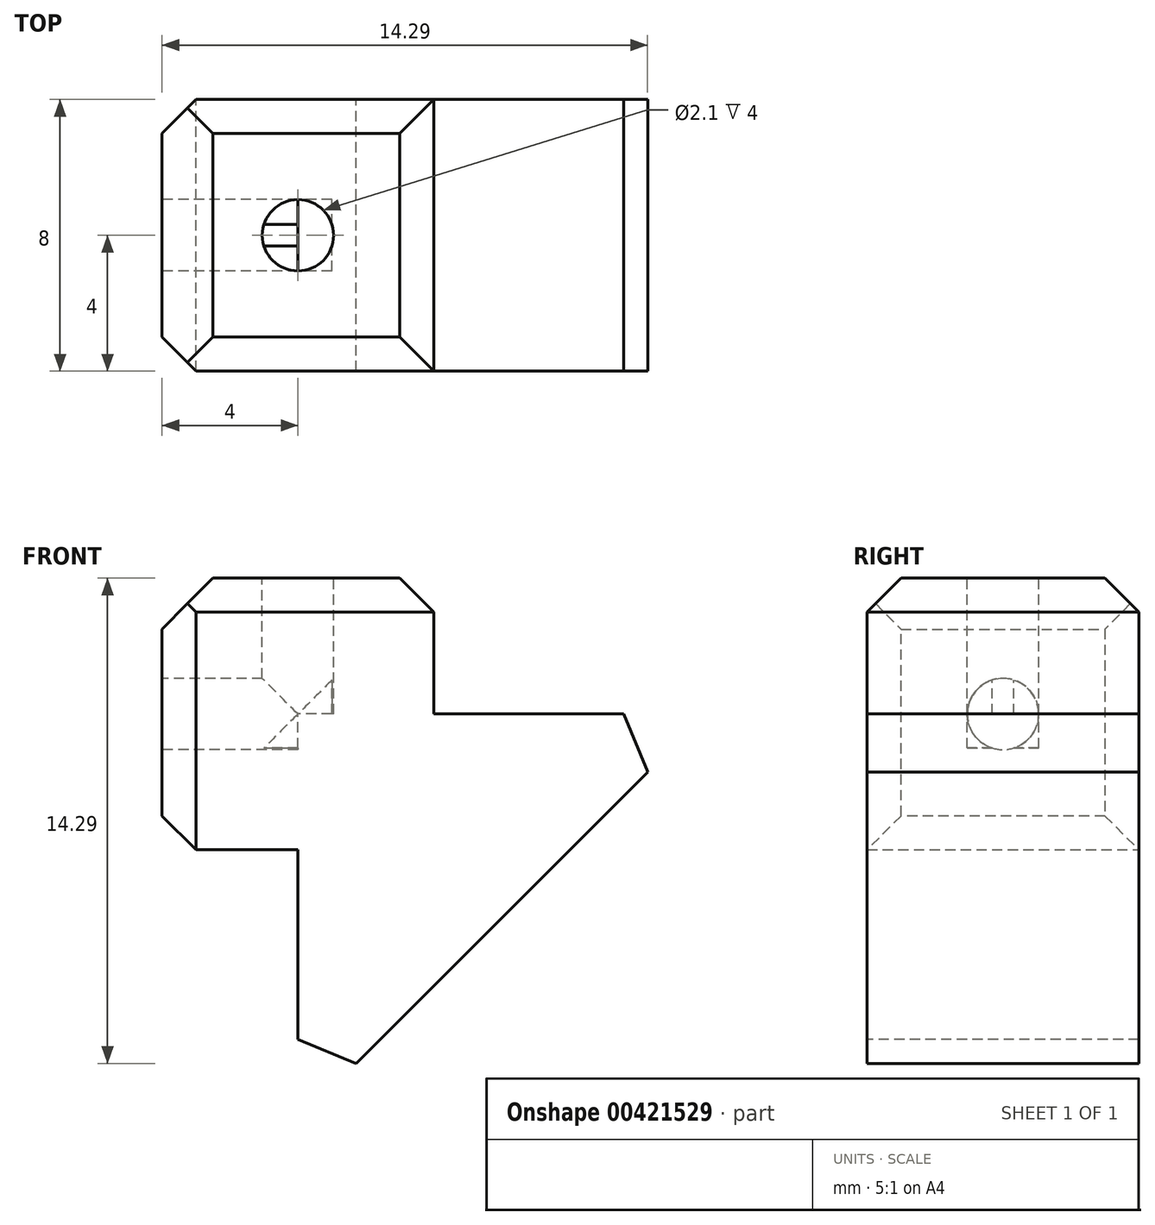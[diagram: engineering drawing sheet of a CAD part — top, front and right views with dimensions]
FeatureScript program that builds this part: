
annotation { "Feature Type Name" : "Feature", "Feature Type Description" : "" }
export const myFeature = defineFeature(function(context is Context, id is Id, definition is map)
    precondition{}
    {
        {
            var Q0;
            Q0=qCreatedBy(makeId("Front.planeOp"),FACE);
            var sketch = newSketch(context, id + "F0", { "sketchPlane" : qUnion([Q0])});
            skLineSegment(sketch, "E0.bottom", {"start": v(4, -4) * mm, "end": v(-4, -4) * mm});
            skLineSegment(sketch, "E0.top", {"start": v(4, 4) * mm, "end": v(-4, 4) * mm});
            skLineSegment(sketch, "E0.left", {"start": v(4, -4) * mm, "end": v(4, 4) * mm});
            skLineSegment(sketch, "E0.right", {"start": v(-4, -4) * mm, "end": v(-4, 4) * mm});
            skPoint(sketch, "E0.middle", {"position": v(0, 0) * mm});
            skSolve(sketch);
        }
        {
            var Q0;
            Q0=makeQuery(id+"F0.imprint","IMPRINT",FACE,{"disambiguationData":[TD([[makeQuery(id+"F0.imprint","IMPRINT",EDGE,{"derivedFrom":sQuery(id+"F0.wireOp",EDGE,"E0.bottom")}),-1.0]])]});
            extrude(context, id + "F1", {"entities" : qUnion([Q0]), "depth" : 8 * mm, "offsetDistance" : 25 * mm, "symmetric" : true});
        }
        {
            var Q0;
            Q0=makeQuery(id+"F1.opExtrude","SWEPT_FACE",FACE,{"disambiguationData":[OSD([sQuery(id+"F0.wireOp",EDGE,"E0.top")])]});
            var sketch = newSketch(context, id + "F2", { "sketchPlane" : qUnion([Q0])});
            skCircle(sketch, "E1", {"center": v(0, 0) * mm, "radius": 1.05 * mm});
            skSolve(sketch);
        }
        {
            var Q0;
            Q0=makeQuery(id+"F2.imprint","IMPRINT",FACE,{"disambiguationData":[TD([[makeQuery(id+"F2.imprint","IMPRINT",EDGE,{"derivedFrom":sQuery(id+"F2.wireOp",EDGE,"E1")}),1.0]])]});
            extrude(context, id + "F3", {"entities" : qUnion([Q0]), "operationType" : NewBodyOperationType.REMOVE, "oppositeDirection" : true, "depth" : 5 * mm, "offsetDistance" : 25 * mm});
        }
        {
            var Q0;
            Q0=makeQuery(id+"F1.opExtrude","SWEPT_FACE",FACE,{"disambiguationData":[OSD([sQuery(id+"F0.wireOp",EDGE,"E0.right")])]});
            var sketch = newSketch(context, id + "F4", { "sketchPlane" : qUnion([Q0])});
            skCircle(sketch, "E2", {"center": v(0, 0) * mm, "radius": 1.05 * mm});
            skSolve(sketch);
        }
        {
            var Q0;
            Q0=makeQuery(id+"F4.imprint","IMPRINT",FACE,{"disambiguationData":[TD([[makeQuery(id+"F4.imprint","IMPRINT",EDGE,{"derivedFrom":sQuery(id+"F4.wireOp",EDGE,"E2")}),1.0]])]});
            extrude(context, id + "F5", {"entities" : qUnion([Q0]), "operationType" : NewBodyOperationType.REMOVE, "oppositeDirection" : true, "depth" : 5 * mm, "offsetDistance" : 25 * mm});
        }
        {
            var Q0;
            Q0=makeQuery(id+"F1.opExtrude","SWEPT_EDGE",EDGE,{"disambiguationData":[OSD([sQuery(id+"F0.wireOp",EDGE,"E0.top"),sQuery(id+"F0.wireOp",EDGE,"E0.right")])]});
            chamfer(context, id + "F6", {"entities" : qUnion([Q0]), "width" : 1.5 * mm, "tangentPropagation" : true});
        }
        {
            var Q0;
            Q0=qCreatedBy(makeId("Front.planeOp"),FACE);
            var sketch = newSketch(context, id + "F7", { "sketchPlane" : qUnion([Q0])});
            skLineSegment(sketch, "E3.bottom", {"start": v(0, 0) * mm, "end": v(12, 0) * mm});
            skLineSegment(sketch, "E3.left", {"start": v(0, 0) * mm, "end": v(0, -12) * mm});
            skLineSegment(sketch, "E4", {"start": v(0, -12) * mm, "end": v(12, 0) * mm});
            skSolve(sketch);
        }
        {
            var Q0;
            Q0=makeQuery(id+"F7.imprint","IMPRINT",FACE,{"disambiguationData":[TD([[makeQuery(id+"F7.imprint","IMPRINT",EDGE,{"derivedFrom":sQuery(id+"F7.wireOp",EDGE,"E3.bottom")}),-1.0]])]});
            extrude(context, id + "F8", {"entities" : qUnion([Q0]), "operationType" : NewBodyOperationType.ADD, "depth" : 8 * mm, "offsetDistance" : 25 * mm, "symmetric" : true});
        }
        {
            var Q0;
            Q0=makeQuery(id+"F8.opExtrude","SWEPT_EDGE",EDGE,{"disambiguationData":[OSD([sQuery(id+"F7.wireOp",EDGE,"E3.bottom"),sQuery(id+"F7.wireOp",EDGE,"E4")])]});
            var Q1;
            Q1=makeQuery(id+"F8.opExtrude","SWEPT_EDGE",EDGE,{"disambiguationData":[OSD([sQuery(id+"F7.wireOp",EDGE,"E3.left"),sQuery(id+"F7.wireOp",EDGE,"E4")])]});
            var Q2;
            Q2=makeQuery(id+"F1.opExtrude","CAP_EDGE",EDGE,{"disambiguationData":[OSD([sQuery(id+"F0.wireOp",EDGE,"E0.top")])],"isStart":false});
            var Q3;
            Q3=makeQuery(id+"F1.opExtrude","CAP_EDGE",EDGE,{"disambiguationData":[OSD([sQuery(id+"F0.wireOp",EDGE,"E0.top")])],"isStart":true});
            var Q4;
            Q4=makeQuery(id+"F1.opExtrude","CAP_EDGE",EDGE,{"disambiguationData":[OSD([sQuery(id+"F0.wireOp",EDGE,"E0.right")])],"isStart":false});
            var Q5;
            Q5=makeQuery(id+"F1.opExtrude","CAP_EDGE",EDGE,{"disambiguationData":[OSD([sQuery(id+"F0.wireOp",EDGE,"E0.right")])],"isStart":true});
            var Q6;
            Q6=makeQuery(id+"F1.opExtrude","SWEPT_EDGE",EDGE,{"disambiguationData":[OSD([sQuery(id+"F0.wireOp",EDGE,"E0.bottom"),sQuery(id+"F0.wireOp",EDGE,"E0.right")])]});
            var Q7;
            Q7=makeQuery(id+"F1.opExtrude","SWEPT_EDGE",EDGE,{"disambiguationData":[OSD([sQuery(id+"F0.wireOp",EDGE,"E0.top"),sQuery(id+"F0.wireOp",EDGE,"E0.left")])]});
            chamfer(context, id + "F9", {"entities" : qUnion([Q0, Q1, Q2, Q3, Q4, Q5, Q6, Q7]), "width" : 1 * mm, "tangentPropagation" : true});
        }
    });
